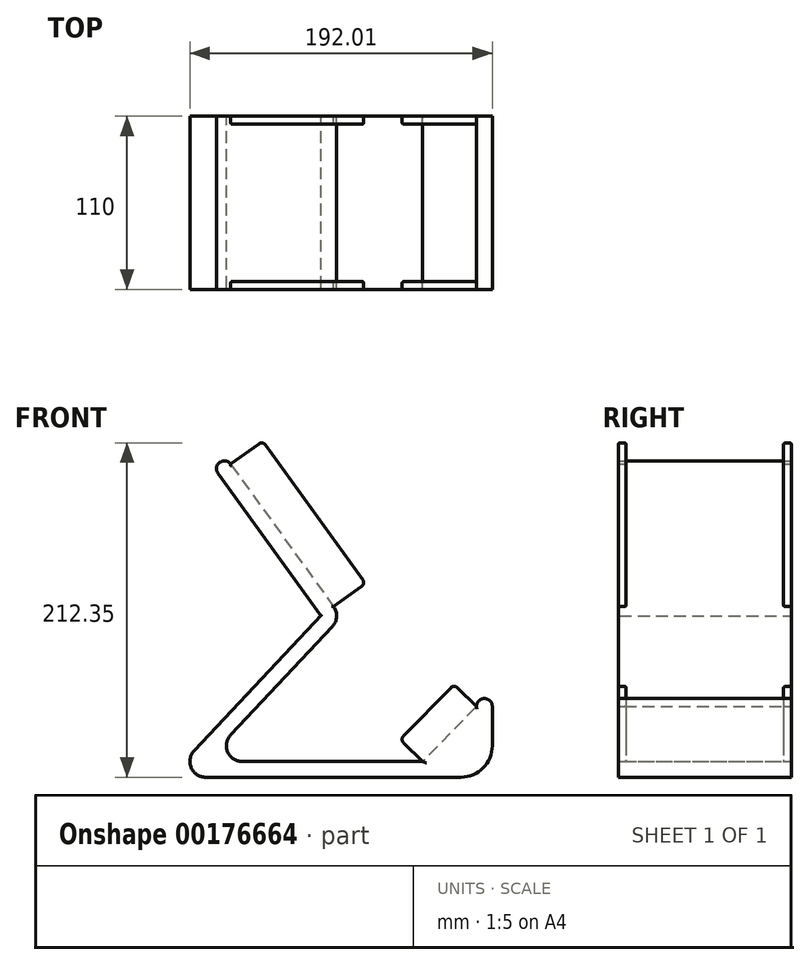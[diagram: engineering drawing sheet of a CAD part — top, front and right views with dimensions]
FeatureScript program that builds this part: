
annotation { "Feature Type Name" : "Feature", "Feature Type Description" : "" }
export const myFeature = defineFeature(function(context is Context, id is Id, definition is map)
    precondition{}
    {
        {
            var Q0;
            Q0=qCreatedBy(makeId("Front.planeOp"),FACE);
            var sketch = newSketch(context, id + "F0", { "sketchPlane" : qUnion([Q0])});
            skLineSegment(sketch, "E0", {"start": v(15.32, -78.97) * mm, "end": v(130, -78.97) * mm});
            skLineSegment(sketch, "E1", {"start": v(65.36, 13.58) * mm, "end": v(0, 104.07) * mm});
            skLineSegment(sketch, "E2", {"start": v(8.03, -62.13) * mm, "end": v(72.65, 6.73) * mm});
            skLineSegment(sketch, "E3.0", {"start": v(73.47, 19.43) * mm, "end": v(8.1, 109.93) * mm});
            skLineSegment(sketch, "E4.0", {"start": v(-15.07, -72.13) * mm, "end": v(63.8, 11.92) * mm});
            skLineSegment(sketch, "E5.0", {"start": v(-7.78, -88.97) * mm, "end": v(154.23, -88.97) * mm});
            skLineSegment(sketch, "E6", {"start": v(63.8, 11.92) * mm, "end": v(65.36, 13.58) * mm});
            skLineSegment(sketch, "E7", {"start": v(174.23, -68.97) * mm, "end": v(174.23, -43.98) * mm});
            skPoint(sketch, "E8.visualSharp", {"position": v(174.23, -88.97) * mm});
            skArc(sketch, "E9.filletArc", {"start": v(154.23, -88.97) * mm, "mid": v(168.37, -83.11) * mm, "end": v(174.23, -68.97) * mm});
            skPoint(sketch, "E10.visualSharp", {"position": v(-30.88, -88.97) * mm});
            skArc(sketch, "E10.filletArc", {"start": v(-15.07, -72.13) * mm, "mid": v(-16.96, -82.94) * mm, "end": v(-7.78, -88.97) * mm});
            skPoint(sketch, "E11.visualSharp", {"position": v(78.3, 12.75) * mm});
            skArc(sketch, "E11.filletArc", {"start": v(72.65, 6.73) * mm, "mid": v(75.34, 12.94) * mm, "end": v(73.47, 19.43) * mm});
            skArc(sketch, "E12.filletArc", {"start": v(8.03, -62.13) * mm, "mid": v(6.14, -72.94) * mm, "end": v(15.32, -78.97) * mm});
            skArc(sketch, "E13", {"start": v(8.1, 109.93) * mm, "mid": v(1.13, 111.06) * mm, "end": v(0, 104.07) * mm});
            skArc(sketch, "E14", {"start": v(174.23, -43.98) * mm, "mid": v(169.23, -38.98) * mm, "end": v(164.23, -43.98) * mm});
            skLineSegment(sketch, "E15", {"start": v(164.23, -43.98) * mm, "end": v(130, -78.97) * mm});
            skSolve(sketch);
        }
        {
            var Q0;
            Q0=makeQuery(id+"F0.imprint","IMPRINT",FACE,{"disambiguationData":[TD([[makeQuery(id+"F0.imprint","IMPRINT",EDGE,{"derivedFrom":sQuery(id+"F0.wireOp",EDGE,"E0")}),-1.0]])]});
            extrude(context, id + "F1", {"entities" : qUnion([Q0]), "depth" : 110 * mm});
        }
        {
            var Q0;
            Q0=makeQuery(id+"F1.opExtrude","SWEPT_FACE",FACE,{"disambiguationData":[OSD([sQuery(id+"F0.wireOp",EDGE,"E3.0")])]});
            var sketch = newSketch(context, id + "F2", { "sketchPlane" : qUnion([Q0])});
            skLineSegment(sketch, "E16", {"start": v(-105, 84.37) * mm, "end": v(-105, -27.26) * mm});
            skLineSegment(sketch, "E17.MirrorCS", {"start": v(-5, 84.37) * mm, "end": v(-5, -27.26) * mm});
            skSolve(sketch);
        }
        {
            var Q0;
            {var subQ0=sQuery(id+"F2.wireOp",EDGE,"E16");Q0=makeQuery(id+"F2.imprint","IMPRINT",FACE,{"disambiguationData":[TD([[makeQuery(id+"F2.imprint","IMPRINT",EDGE,{"derivedFrom":subQ0}),-1.0]])]});}
            var Q1;
            {var subQ0=sQuery(id+"F2.wireOp",EDGE,"E17.MirrorCS");Q1=makeQuery(id+"F2.imprint","IMPRINT",FACE,{"disambiguationData":[TD([[makeQuery(id+"F2.imprint","IMPRINT",EDGE,{"derivedFrom":subQ0}),1.0]])]});}
            extrude(context, id + "F3", {"entities" : qUnion([Q0, Q1]), "operationType" : NewBodyOperationType.ADD, "depth" : 25 * mm});
        }
        {
            var Q0;
            {var subQ0=sQuery(id+"F0.wireOp",EDGE,"E3.0");var subQ1=sQuery(id+"F0.wireOp",EDGE,"E11.filletArc");var subQ2=makeQuery(id+"F1.opExtrude","SWEPT_EDGE",EDGE,{"disambiguationData":[OSD([subQ0,subQ1])]});Q0=makeQuery(id+"F3.opExtrude","CAP_EDGE",EDGE,{"disambiguationData":[OSD([subQ0,subQ1]),TDD([makeQuery(id+"F2.imprint","IMPRINT",EDGE,{"disambiguationData":[TD([[makeQuery(id+"F2.imprint","INTERSECT",VERTEX,{"derivedFrom":[subQ2,makeQuery(id+"F1.opExtrude","CAP_EDGE",EDGE,{"disambiguationData":[OSD([subQ0])],"isStart":false})]}),-1.0]])],"derivedFrom":subQ2})])],"isStart":false});}
            var Q1;
            {var subQ0=sQuery(id+"F0.wireOp",EDGE,"E3.0");var subQ1=sQuery(id+"F0.wireOp",EDGE,"E11.filletArc");var subQ2=makeQuery(id+"F1.opExtrude","SWEPT_EDGE",EDGE,{"disambiguationData":[OSD([subQ0,subQ1])]});Q1=makeQuery(id+"F3.opExtrude","CAP_EDGE",EDGE,{"disambiguationData":[OSD([subQ0,subQ1]),TDD([makeQuery(id+"F2.imprint","IMPRINT",EDGE,{"disambiguationData":[TD([[makeQuery(id+"F2.imprint","INTERSECT",VERTEX,{"derivedFrom":[subQ2,makeQuery(id+"F1.opExtrude","CAP_EDGE",EDGE,{"disambiguationData":[OSD([subQ0])],"isStart":true})]}),1.0]])],"derivedFrom":subQ2})])],"isStart":false});}
            var Q2;
            {var subQ0=sQuery(id+"F0.wireOp",EDGE,"E3.0");var subQ1=sQuery(id+"F0.wireOp",EDGE,"E13");var subQ2=makeQuery(id+"F1.opExtrude","SWEPT_EDGE",EDGE,{"disambiguationData":[OSD([subQ0,subQ1])]});Q2=makeQuery(id+"F3.opExtrude","CAP_EDGE",EDGE,{"disambiguationData":[OSD([subQ0,subQ1]),TDD([makeQuery(id+"F2.imprint","IMPRINT",EDGE,{"disambiguationData":[TD([[makeQuery(id+"F2.imprint","INTERSECT",VERTEX,{"derivedFrom":[subQ2,makeQuery(id+"F1.opExtrude","CAP_EDGE",EDGE,{"disambiguationData":[OSD([subQ0])],"isStart":false})]}),-1.0]])],"derivedFrom":subQ2})])],"isStart":false});}
            var Q3;
            {var subQ0=sQuery(id+"F0.wireOp",EDGE,"E3.0");var subQ1=sQuery(id+"F0.wireOp",EDGE,"E13");var subQ2=makeQuery(id+"F1.opExtrude","SWEPT_EDGE",EDGE,{"disambiguationData":[OSD([subQ0,subQ1])]});Q3=makeQuery(id+"F3.opExtrude","CAP_EDGE",EDGE,{"disambiguationData":[OSD([subQ0,subQ1]),TDD([makeQuery(id+"F2.imprint","IMPRINT",EDGE,{"disambiguationData":[TD([[makeQuery(id+"F2.imprint","INTERSECT",VERTEX,{"derivedFrom":[subQ2,makeQuery(id+"F1.opExtrude","CAP_EDGE",EDGE,{"disambiguationData":[OSD([subQ0])],"isStart":true})]}),1.0]])],"derivedFrom":subQ2})])],"isStart":false});}
            fillet(context, id + "F4", {"entities" : qUnion([Q0, Q1, Q2, Q3]), "radius" : 3 * mm, "tangentPropagation" : true, "allowEdgeOverflow" : false});
        }
        {
            var Q0;
            {var subQ0=sQuery(id+"F0.wireOp",EDGE,"E3.0");var subQ1=sQuery(id+"F0.wireOp",EDGE,"E13");Q0=makeQuery(id+"F3.opExtrude","SWEPT_EDGE",EDGE,{"disambiguationData":[OSD([subQ0,subQ1]),TDD([makeQuery(id+"F2.imprint","INTERSECT",VERTEX,{"derivedFrom":[makeQuery(id+"F1.opExtrude","SWEPT_EDGE",EDGE,{"disambiguationData":[OSD([subQ0,subQ1])]}),makeQuery(id+"F1.opExtrude","CAP_EDGE",EDGE,{"disambiguationData":[OSD([subQ0])],"isStart":false})]})])]});}
            var Q1;
            Q1=makeQuery(id+"F1.opExtrude","CAP_EDGE",EDGE,{"disambiguationData":[OSD([sQuery(id+"F0.wireOp",EDGE,"E1")])],"isStart":false});
            var Q2;
            Q2=makeQuery(id+"F3.opExtrude","CAP_EDGE",EDGE,{"disambiguationData":[OSD([sQuery(id+"F2.wireOp",EDGE,"E16")])],"isStart":false});
            var Q3;
            Q3=makeQuery(id+"F3.opExtrude","CAP_EDGE",EDGE,{"disambiguationData":[OSD([sQuery(id+"F2.wireOp",EDGE,"E17.MirrorCS")])],"isStart":false});
            var Q4;
            {var subQ0=sQuery(id+"F0.wireOp",EDGE,"E3.0");Q4=makeQuery(id+"F3.opExtrude","CAP_EDGE",EDGE,{"disambiguationData":[OSD([subQ0]),TDD([makeQuery(id+"F2.imprint","IMPRINT",EDGE,{"derivedFrom":makeQuery(id+"F1.opExtrude","CAP_EDGE",EDGE,{"disambiguationData":[OSD([subQ0])],"isStart":true})})])],"isStart":false});}
            var Q5;
            Q5=makeQuery(id+"F1.opExtrude","CAP_EDGE",EDGE,{"disambiguationData":[OSD([sQuery(id+"F0.wireOp",EDGE,"E1")])],"isStart":true});
            fillet(context, id + "F5", {"entities" : qUnion([Q0, Q1, Q2, Q3, Q4, Q5]), "radius" : 1 * mm, "tangentPropagation" : true, "allowEdgeOverflow" : false});
        }
        {
            var Q0;
            Q0=makeQuery(id+"F1.opExtrude","SWEPT_FACE",FACE,{"disambiguationData":[OSD([sQuery(id+"F0.wireOp",EDGE,"E15")])]});
            var sketch = newSketch(context, id + "F6", { "sketchPlane" : qUnion([Q0])});
            skLineSegment(sketch, "E18", {"start": v(5, 83.4) * mm, "end": v(5, 34.46) * mm});
            skLineSegment(sketch, "E19.MirrorCS", {"start": v(105, 83.4) * mm, "end": v(105, 34.46) * mm});
            skSolve(sketch);
        }
        {
            var Q0;
            {var subQ0=sQuery(id+"F6.wireOp",EDGE,"E18");Q0=makeQuery(id+"F6.imprint","IMPRINT",FACE,{"disambiguationData":[TD([[makeQuery(id+"F6.imprint","IMPRINT",EDGE,{"derivedFrom":subQ0}),-1.0]])]});}
            var Q1;
            {var subQ0=sQuery(id+"F6.wireOp",EDGE,"E19.MirrorCS");Q1=makeQuery(id+"F6.imprint","IMPRINT",FACE,{"disambiguationData":[TD([[makeQuery(id+"F6.imprint","IMPRINT",EDGE,{"derivedFrom":subQ0}),1.0]])]});}
            extrude(context, id + "F7", {"entities" : qUnion([Q0, Q1]), "operationType" : NewBodyOperationType.ADD, "depth" : 20 * mm});
        }
        {
            var Q0;
            {var subQ0=sQuery(id+"F0.wireOp",EDGE,"E15");var subQ1=sQuery(id+"F0.wireOp",EDGE,"E14");var subQ2=makeQuery(id+"F1.opExtrude","SWEPT_EDGE",EDGE,{"disambiguationData":[OSD([subQ1,subQ0])]});Q0=makeQuery(id+"F7.opExtrude","CAP_EDGE",EDGE,{"disambiguationData":[OSD([subQ1,subQ0]),TDD([makeQuery(id+"F6.imprint","IMPRINT",EDGE,{"disambiguationData":[TD([[makeQuery(id+"F6.imprint","INTERSECT",VERTEX,{"derivedFrom":[subQ2,makeQuery(id+"F1.opExtrude","CAP_EDGE",EDGE,{"disambiguationData":[OSD([subQ0])],"isStart":true})]}),1.0]])],"derivedFrom":subQ2})])],"isStart":false});}
            var Q1;
            {var subQ0=sQuery(id+"F0.wireOp",EDGE,"E15");var subQ1=sQuery(id+"F0.wireOp",EDGE,"E0");var subQ2=makeQuery(id+"F1.opExtrude","SWEPT_EDGE",EDGE,{"disambiguationData":[OSD([subQ1,subQ0])]});Q1=makeQuery(id+"F7.opExtrude","CAP_EDGE",EDGE,{"disambiguationData":[OSD([subQ1,subQ0]),TDD([makeQuery(id+"F6.imprint","IMPRINT",EDGE,{"disambiguationData":[TD([[makeQuery(id+"F6.imprint","INTERSECT",VERTEX,{"derivedFrom":[subQ2,makeQuery(id+"F1.opExtrude","CAP_EDGE",EDGE,{"disambiguationData":[OSD([subQ0])],"isStart":true})]}),1.0]])],"derivedFrom":subQ2})])],"isStart":false});}
            var Q2;
            {var subQ0=sQuery(id+"F0.wireOp",EDGE,"E15");var subQ1=sQuery(id+"F0.wireOp",EDGE,"E0");var subQ2=makeQuery(id+"F1.opExtrude","SWEPT_EDGE",EDGE,{"disambiguationData":[OSD([subQ1,subQ0])]});Q2=makeQuery(id+"F7.opExtrude","CAP_EDGE",EDGE,{"disambiguationData":[OSD([subQ1,subQ0]),TDD([makeQuery(id+"F6.imprint","IMPRINT",EDGE,{"disambiguationData":[TD([[makeQuery(id+"F6.imprint","INTERSECT",VERTEX,{"derivedFrom":[subQ2,makeQuery(id+"F1.opExtrude","CAP_EDGE",EDGE,{"disambiguationData":[OSD([subQ0])],"isStart":false})]}),-1.0]])],"derivedFrom":subQ2})])],"isStart":false});}
            var Q3;
            {var subQ0=sQuery(id+"F0.wireOp",EDGE,"E15");var subQ1=sQuery(id+"F0.wireOp",EDGE,"E14");var subQ2=makeQuery(id+"F1.opExtrude","SWEPT_EDGE",EDGE,{"disambiguationData":[OSD([subQ1,subQ0])]});Q3=makeQuery(id+"F7.opExtrude","CAP_EDGE",EDGE,{"disambiguationData":[OSD([subQ1,subQ0]),TDD([makeQuery(id+"F6.imprint","IMPRINT",EDGE,{"disambiguationData":[TD([[makeQuery(id+"F6.imprint","INTERSECT",VERTEX,{"derivedFrom":[subQ2,makeQuery(id+"F1.opExtrude","CAP_EDGE",EDGE,{"disambiguationData":[OSD([subQ0])],"isStart":false})]}),-1.0]])],"derivedFrom":subQ2})])],"isStart":false});}
            fillet(context, id + "F8", {"entities" : qUnion([Q0, Q1, Q2, Q3]), "radius" : 3 * mm, "tangentPropagation" : true, "allowEdgeOverflow" : false});
        }
        {
            var Q0;
            {var subQ0=sQuery(id+"F0.wireOp",EDGE,"E15");var subQ1=sQuery(id+"F0.wireOp",EDGE,"E14");Q0=makeQuery(id+"F7.opExtrude","SWEPT_EDGE",EDGE,{"disambiguationData":[OSD([subQ1,subQ0]),TDD([makeQuery(id+"F6.imprint","INTERSECT",VERTEX,{"derivedFrom":[makeQuery(id+"F1.opExtrude","SWEPT_EDGE",EDGE,{"disambiguationData":[OSD([subQ1,subQ0])]}),makeQuery(id+"F1.opExtrude","CAP_EDGE",EDGE,{"disambiguationData":[OSD([subQ0])],"isStart":true})]})])]});}
            var Q1;
            {var subQ0=sQuery(id+"F0.wireOp",EDGE,"E15");var subQ1=sQuery(id+"F0.wireOp",EDGE,"E0");Q1=makeQuery(id+"F7.opExtrude","SWEPT_EDGE",EDGE,{"disambiguationData":[OSD([subQ1,subQ0]),TDD([makeQuery(id+"F6.imprint","INTERSECT",VERTEX,{"derivedFrom":[makeQuery(id+"F1.opExtrude","SWEPT_EDGE",EDGE,{"disambiguationData":[OSD([subQ1,subQ0])]}),makeQuery(id+"F1.opExtrude","CAP_EDGE",EDGE,{"disambiguationData":[OSD([subQ0])],"isStart":true})]})])]});}
            var Q2;
            Q2=makeQuery(id+"F7.opExtrude","SWEPT_EDGE",EDGE,{"disambiguationData":[OSD([sQuery(id+"F0.wireOp",EDGE,"E0"),sQuery(id+"F0.wireOp",EDGE,"E15"),sQuery(id+"F6.wireOp",EDGE,"E19.MirrorCS")])]});
            var Q3;
            Q3=makeQuery(id+"F7.opExtrude","SWEPT_EDGE",EDGE,{"disambiguationData":[OSD([sQuery(id+"F0.wireOp",EDGE,"E14"),sQuery(id+"F0.wireOp",EDGE,"E15"),sQuery(id+"F6.wireOp",EDGE,"E18")])]});
            var Q4;
            Q4=makeQuery(id+"F7.opExtrude","CAP_EDGE",EDGE,{"disambiguationData":[OSD([sQuery(id+"F6.wireOp",EDGE,"E18")])],"isStart":false});
            var Q5;
            {var subQ0=sQuery(id+"F0.wireOp",EDGE,"E15");Q5=makeQuery(id+"F7.opExtrude","CAP_EDGE",EDGE,{"disambiguationData":[OSD([subQ0]),TDD([makeQuery(id+"F6.imprint","IMPRINT",EDGE,{"derivedFrom":makeQuery(id+"F1.opExtrude","CAP_EDGE",EDGE,{"disambiguationData":[OSD([subQ0])],"isStart":false})})])],"isStart":false});}
            var Q6;
            {var subQ0=sQuery(id+"F0.wireOp",EDGE,"E15");var subQ1=sQuery(id+"F0.wireOp",EDGE,"E14");Q6=makeQuery(id+"F7.opExtrude","SWEPT_EDGE",EDGE,{"disambiguationData":[OSD([subQ1,subQ0]),TDD([makeQuery(id+"F6.imprint","INTERSECT",VERTEX,{"derivedFrom":[makeQuery(id+"F1.opExtrude","SWEPT_EDGE",EDGE,{"disambiguationData":[OSD([subQ1,subQ0])]}),makeQuery(id+"F1.opExtrude","CAP_EDGE",EDGE,{"disambiguationData":[OSD([subQ0])],"isStart":false})]})])]});}
            var Q7;
            {var subQ0=sQuery(id+"F0.wireOp",EDGE,"E15");var subQ1=sQuery(id+"F0.wireOp",EDGE,"E0");Q7=makeQuery(id+"F7.opExtrude","SWEPT_EDGE",EDGE,{"disambiguationData":[OSD([subQ1,subQ0]),TDD([makeQuery(id+"F6.imprint","INTERSECT",VERTEX,{"derivedFrom":[makeQuery(id+"F1.opExtrude","SWEPT_EDGE",EDGE,{"disambiguationData":[OSD([subQ1,subQ0])]}),makeQuery(id+"F1.opExtrude","CAP_EDGE",EDGE,{"disambiguationData":[OSD([subQ0])],"isStart":false})]})])]});}
            fillet(context, id + "F9", {"entities" : qUnion([Q0, Q1, Q2, Q3, Q4, Q5, Q6, Q7]), "radius" : 1 * mm, "tangentPropagation" : true, "allowEdgeOverflow" : false});
        }
        {
            var Q0;
            Q0=makeQuery(id+"F1.opExtrude","CAP_EDGE",EDGE,{"disambiguationData":[OSD([sQuery(id+"F0.wireOp",EDGE,"E0")])],"isStart":false});
            var Q1;
            Q1=makeQuery(id+"F1.opExtrude","CAP_EDGE",EDGE,{"disambiguationData":[OSD([sQuery(id+"F0.wireOp",EDGE,"E0")])],"isStart":true});
            fillet(context, id + "F10", {"entities" : qUnion([Q0, Q1]), "radius" : 1 * mm, "tangentPropagation" : true, "allowEdgeOverflow" : false});
        }
    });
